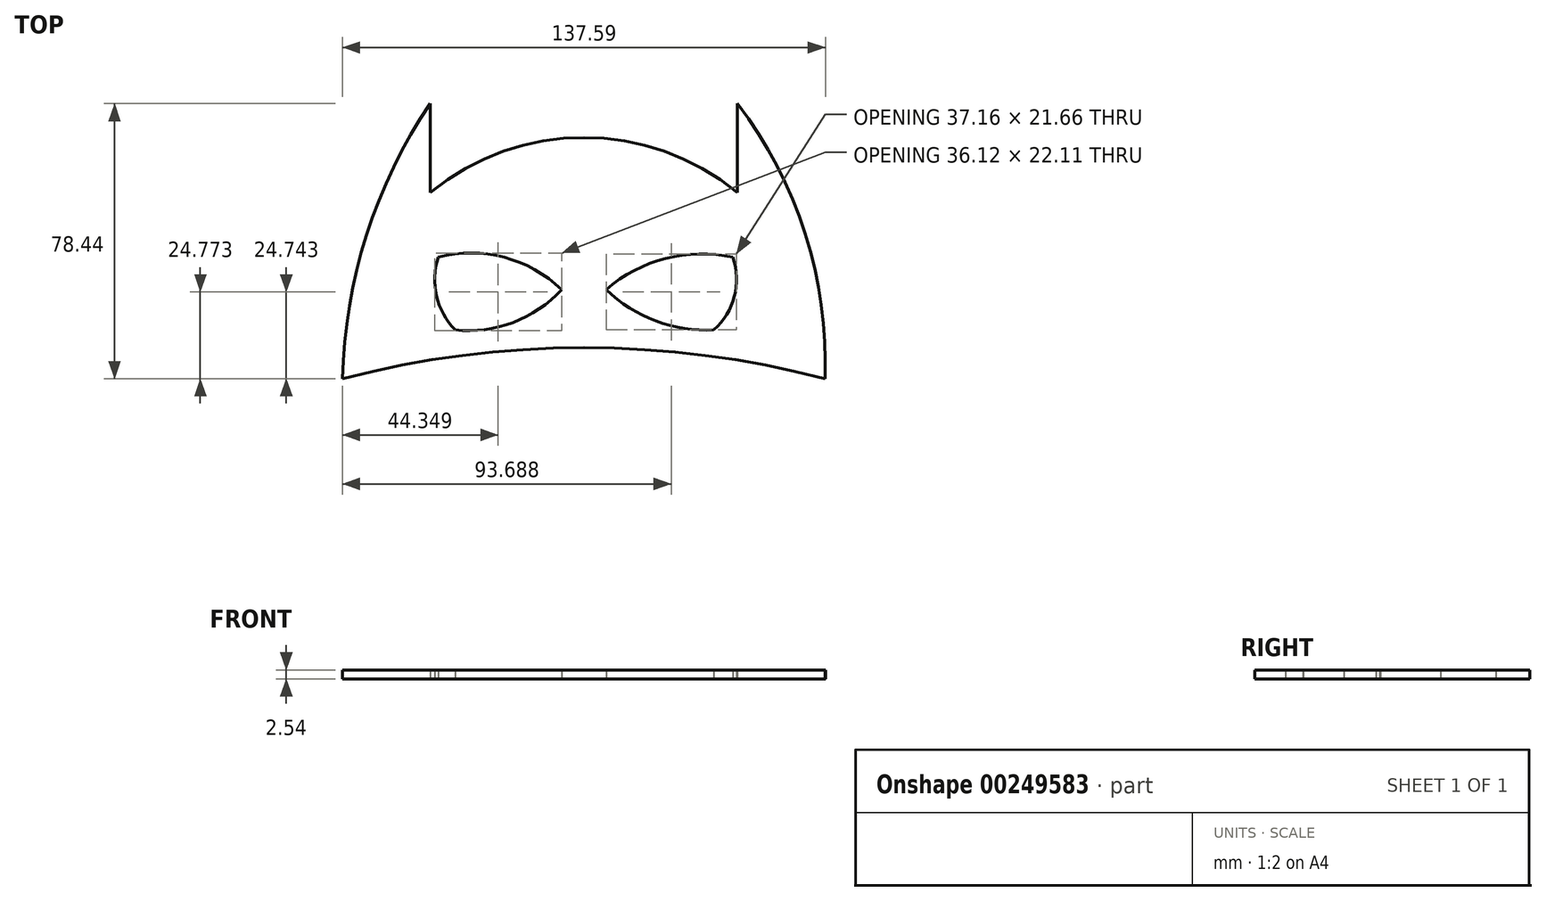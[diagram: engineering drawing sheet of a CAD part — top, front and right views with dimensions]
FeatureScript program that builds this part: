
annotation { "Feature Type Name" : "Feature", "Feature Type Description" : "" }
export const myFeature = defineFeature(function(context is Context, id is Id, definition is map)
    precondition{}
    {
        {
            var Q0;
            Q0=qCreatedBy(makeId("Top.planeOp"),FACE);
            var sketch = newSketch(context, id + "F0", { "sketchPlane" : qUnion([Q0])});
            skArc(sketch, "E0", {"start": v(43.75, 53.04) * mm, "mid": v(0, 68.76) * mm, "end": v(-43.75, 53.04) * mm});
            skArc(sketch, "E1", {"start": v(68.76, 0) * mm, "mid": v(0, 8.86) * mm, "end": v(-68.76, 0) * mm});
            skLineSegment(sketch, "E2", {"start": v(-43.75, 53.04) * mm, "end": v(-43.75, 78.44) * mm});
            skLineSegment(sketch, "E3", {"start": v(-43.75, 78.44) * mm, "end": v(43.75, 78.44) * mm});
            skLineSegment(sketch, "E4", {"start": v(43.75, 78.44) * mm, "end": v(43.75, 53.04) * mm});
            skArc(sketch, "E5", {"start": v(-43.75, 78.44) * mm, "mid": v(-61.92, 41.03) * mm, "end": v(-68.76, 0) * mm});
            skArc(sketch, "E6", {"start": v(68.76, 0) * mm, "mid": v(63.04, 41.38) * mm, "end": v(43.75, 78.44) * mm});
            skArc(sketch, "E7", {"start": v(42.46, 34.6) * mm, "mid": v(23.31, 34.3) * mm, "end": v(6.35, 25.4) * mm});
            skArc(sketch, "E8", {"start": v(37.05, 13.92) * mm, "mid": v(42.9, 23.44) * mm, "end": v(42.46, 34.6) * mm});
            skArc(sketch, "E9", {"start": v(6.35, 25.4) * mm, "mid": v(20.5, 16.47) * mm, "end": v(37.05, 13.92) * mm});
            skArc(sketch, "E10", {"start": v(-6.35, 25.4) * mm, "mid": v(-22.71, 34.62) * mm, "end": v(-41.5, 34.6) * mm});
            skArc(sketch, "E11", {"start": v(-41.5, 34.6) * mm, "mid": v(-41.96, 23.6) * mm, "end": v(-36.7, 13.92) * mm});
            skArc(sketch, "E12", {"start": v(-36.7, 13.92) * mm, "mid": v(-20.16, 16.05) * mm, "end": v(-6.35, 25.4) * mm});
            skArc(sketch, "E13.trimOffspring", {"start": v(-68.53, 5.63) * mm, "mid": v(-68.7, 2.82) * mm, "end": v(-68.76, 0) * mm});
            skSolve(sketch);
        }
        {
            var Q0;
            Q0=makeQuery(id+"F0.imprint","IMPRINT",FACE,{"disambiguationData":[TD([[makeQuery(id+"F0.imprint","IMPRINT",EDGE,{"derivedFrom":sQuery(id+"F0.wireOp",EDGE,"E0")}),1.0]])]});
            extrude(context, id + "F1", {"entities" : qUnion([Q0]), "depth" : 2.54 * mm});
        }
    });
